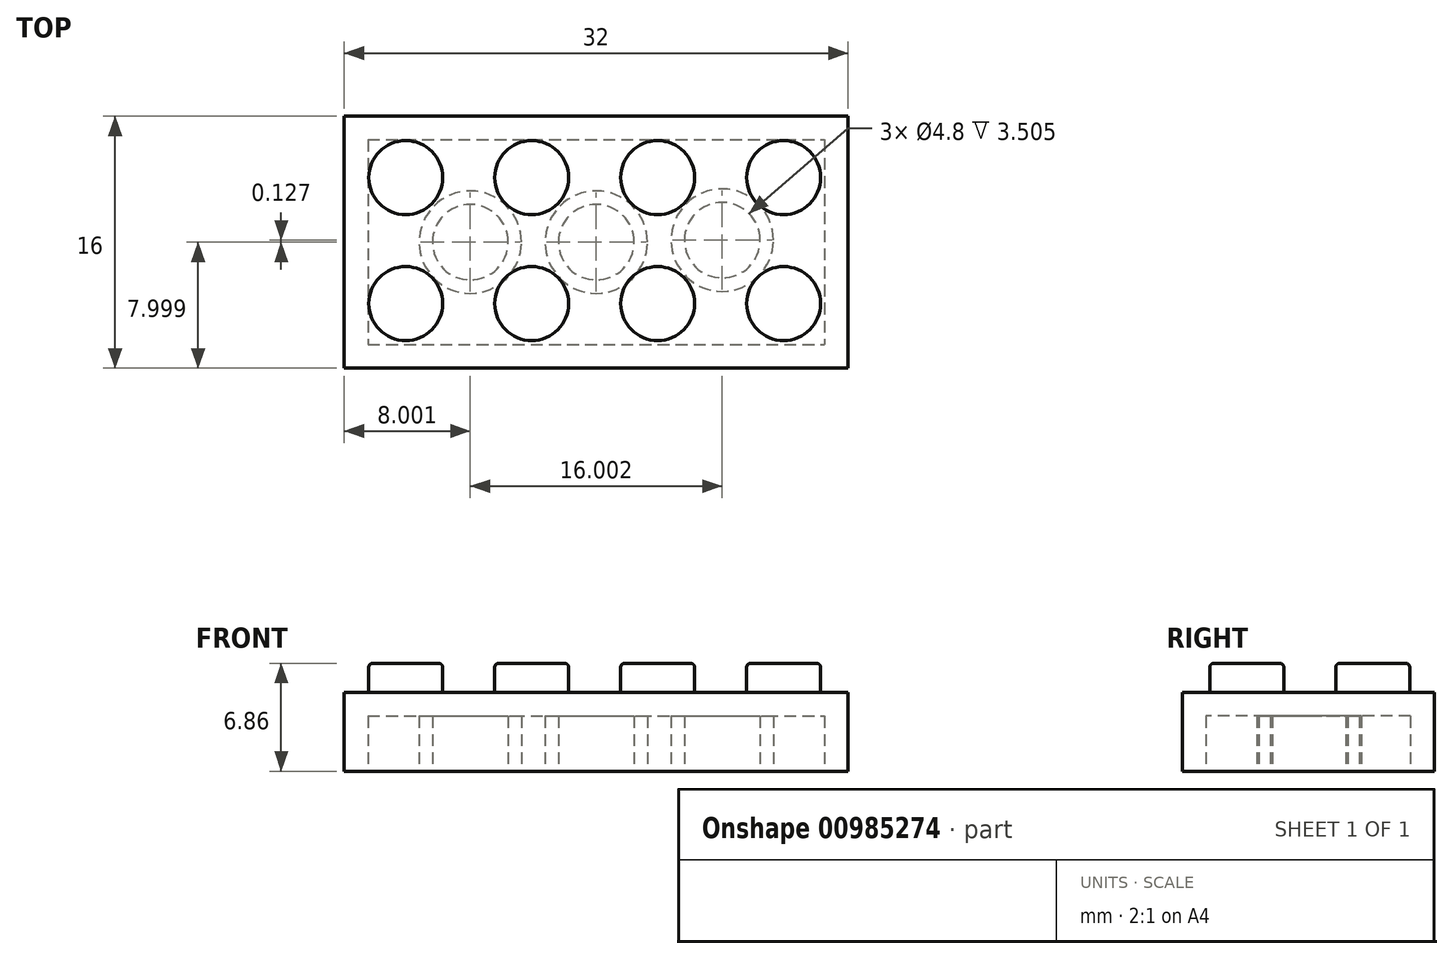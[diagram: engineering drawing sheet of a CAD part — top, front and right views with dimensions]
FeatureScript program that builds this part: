
annotation { "Feature Type Name" : "Feature", "Feature Type Description" : "" }
export const myFeature = defineFeature(function(context is Context, id is Id, definition is map)
    precondition{}
    {
        {
            var Q0;
            Q0=qCreatedBy(makeId("Top.planeOp"),FACE);
            var sketch = newSketch(context, id + "F0", { "sketchPlane" : qUnion([Q0])});
            skLineSegment(sketch, "E0.bottom", {"start": v(0, 0) * mm, "end": v(32, 0) * mm});
            skLineSegment(sketch, "E0.top", {"start": v(0, -16) * mm, "end": v(32, -16) * mm});
            skLineSegment(sketch, "E0.left", {"start": v(0, 0) * mm, "end": v(0, -16) * mm});
            skLineSegment(sketch, "E0.right", {"start": v(32, 0) * mm, "end": v(32, -16) * mm});
            skSolve(sketch);
        }
        {
            var Q0;
            Q0=makeQuery(id+"F0.imprint","IMPRINT",FACE,{"disambiguationData":[TD([[makeQuery(id+"F0.imprint","IMPRINT",EDGE,{"derivedFrom":sQuery(id+"F0.wireOp",EDGE,"E0.bottom")}),-1.0]])]});
            extrude(context, id + "F1", {"entities" : qUnion([Q0]), "depth" : 5 * mm, "offsetDistance" : 25.4 * mm});
        }
        {
            var Q0;
            Q0=makeQuery(id+"F1.opExtrude","CAP_FACE",FACE,{"disambiguationData":[OSD([sQuery(id+"F0.wireOp",EDGE,"E0.bottom"),sQuery(id+"F0.wireOp",EDGE,"E0.top"),sQuery(id+"F0.wireOp",EDGE,"E0.left"),sQuery(id+"F0.wireOp",EDGE,"E0.right")])],"isStart":false});
            var sketch = newSketch(context, id + "F2", { "sketchPlane" : qUnion([Q0])});
            skCircle(sketch, "E1", {"center": v(3.9, -3.9) * mm, "radius": 2.35 * mm});
            skCircle(sketch, "E2.0.1.0", {"center": v(3.9, -11.9) * mm, "radius": 2.35 * mm});
            skCircle(sketch, "E2.1.0.0", {"center": v(11.9, -3.9) * mm, "radius": 2.35 * mm});
            skCircle(sketch, "E2.1.1.0", {"center": v(11.9, -11.9) * mm, "radius": 2.35 * mm});
            skCircle(sketch, "E2.2.0.0", {"center": v(19.9, -3.9) * mm, "radius": 2.35 * mm});
            skCircle(sketch, "E2.2.1.0", {"center": v(19.9, -11.9) * mm, "radius": 2.35 * mm});
            skCircle(sketch, "E2.3.0.0", {"center": v(27.9, -3.9) * mm, "radius": 2.35 * mm});
            skCircle(sketch, "E2.3.1.0", {"center": v(27.9, -11.9) * mm, "radius": 2.35 * mm});
            skLineSegment(sketch, "E2.direction1", {"start": v(3.9, -3.9) * mm, "end": v(11.9, -3.9) * mm, "construction": true});
            skLineSegment(sketch, "E2.direction2", {"start": v(3.9, -3.9) * mm, "end": v(3.9, -11.9) * mm, "construction": true});
            skSolve(sketch);
        }
        {
            var Q0;
            Q0=makeQuery(id+"F2.imprint","IMPRINT",FACE,{"disambiguationData":[TD([[makeQuery(id+"F2.imprint","IMPRINT",EDGE,{"derivedFrom":sQuery(id+"F2.wireOp",EDGE,"E1")}),1.0]])]});
            var Q1;
            Q1=makeQuery(id+"F2.imprint","IMPRINT",FACE,{"disambiguationData":[TD([[makeQuery(id+"F2.imprint","IMPRINT",EDGE,{"derivedFrom":sQuery(id+"F2.wireOp",EDGE,"E2.1.0.0")}),1.0]])]});
            var Q2;
            Q2=makeQuery(id+"F2.imprint","IMPRINT",FACE,{"disambiguationData":[TD([[makeQuery(id+"F2.imprint","IMPRINT",EDGE,{"derivedFrom":sQuery(id+"F2.wireOp",EDGE,"E2.2.0.0")}),1.0]])]});
            var Q3;
            Q3=makeQuery(id+"F2.imprint","IMPRINT",FACE,{"disambiguationData":[TD([[makeQuery(id+"F2.imprint","IMPRINT",EDGE,{"derivedFrom":sQuery(id+"F2.wireOp",EDGE,"E2.3.0.0")}),1.0]])]});
            var Q4;
            Q4=makeQuery(id+"F2.imprint","IMPRINT",FACE,{"disambiguationData":[TD([[makeQuery(id+"F2.imprint","IMPRINT",EDGE,{"derivedFrom":sQuery(id+"F2.wireOp",EDGE,"E2.3.1.0")}),1.0]])]});
            var Q5;
            Q5=makeQuery(id+"F2.imprint","IMPRINT",FACE,{"disambiguationData":[TD([[makeQuery(id+"F2.imprint","IMPRINT",EDGE,{"derivedFrom":sQuery(id+"F2.wireOp",EDGE,"E2.2.1.0")}),1.0]])]});
            var Q6;
            Q6=makeQuery(id+"F2.imprint","IMPRINT",FACE,{"disambiguationData":[TD([[makeQuery(id+"F2.imprint","IMPRINT",EDGE,{"derivedFrom":sQuery(id+"F2.wireOp",EDGE,"E2.1.1.0")}),1.0]])]});
            var Q7;
            Q7=makeQuery(id+"F2.imprint","IMPRINT",FACE,{"disambiguationData":[TD([[makeQuery(id+"F2.imprint","IMPRINT",EDGE,{"derivedFrom":sQuery(id+"F2.wireOp",EDGE,"E2.0.1.0")}),1.0]])]});
            extrude(context, id + "F3", {"entities" : qUnion([Q0, Q1, Q2, Q3, Q4, Q5, Q6, Q7]), "operationType" : NewBodyOperationType.ADD, "depth" : 1.85 * mm, "offsetDistance" : 25.4 * mm});
        }
        {
            var Q0;
            Q0=makeQuery(id+"F3.opExtrude","CAP_EDGE",EDGE,{"disambiguationData":[OSD([sQuery(id+"F2.wireOp",EDGE,"E2.0.1.0")])],"isStart":false});
            var Q1;
            Q1=makeQuery(id+"F3.opExtrude","CAP_EDGE",EDGE,{"disambiguationData":[OSD([sQuery(id+"F2.wireOp",EDGE,"E1")])],"isStart":false});
            var Q2;
            Q2=makeQuery(id+"F3.opExtrude","CAP_EDGE",EDGE,{"disambiguationData":[OSD([sQuery(id+"F2.wireOp",EDGE,"E2.1.0.0")])],"isStart":false});
            var Q3;
            Q3=makeQuery(id+"F3.opExtrude","CAP_EDGE",EDGE,{"disambiguationData":[OSD([sQuery(id+"F2.wireOp",EDGE,"E2.1.1.0")])],"isStart":false});
            var Q4;
            Q4=makeQuery(id+"F3.opExtrude","CAP_EDGE",EDGE,{"disambiguationData":[OSD([sQuery(id+"F2.wireOp",EDGE,"E2.2.1.0")])],"isStart":false});
            var Q5;
            Q5=makeQuery(id+"F3.opExtrude","CAP_EDGE",EDGE,{"disambiguationData":[OSD([sQuery(id+"F2.wireOp",EDGE,"E2.2.0.0")])],"isStart":false});
            var Q6;
            Q6=makeQuery(id+"F3.opExtrude","CAP_EDGE",EDGE,{"disambiguationData":[OSD([sQuery(id+"F2.wireOp",EDGE,"E2.3.0.0")])],"isStart":false});
            var Q7;
            Q7=makeQuery(id+"F3.opExtrude","CAP_EDGE",EDGE,{"disambiguationData":[OSD([sQuery(id+"F2.wireOp",EDGE,"E2.3.1.0")])],"isStart":false});
            fillet(context, id + "F4", {"entities" : qUnion([Q0, Q1, Q2, Q3, Q4, Q5, Q6, Q7]), "radius" : 0.25 * mm, "tangentPropagation" : true, "allowEdgeOverflow" : false});
        }
        {
            var Q0;
            Q0=makeQuery(id+"F1.opExtrude","CAP_FACE",FACE,{"disambiguationData":[OSD([sQuery(id+"F0.wireOp",EDGE,"E0.bottom"),sQuery(id+"F0.wireOp",EDGE,"E0.top"),sQuery(id+"F0.wireOp",EDGE,"E0.left"),sQuery(id+"F0.wireOp",EDGE,"E0.right")])],"isStart":true});
            var sketch = newSketch(context, id + "F5", { "sketchPlane" : qUnion([Q0])});
            skLineSegment(sketch, "E3.0", {"start": v(1.5, 14.5) * mm, "end": v(30.5, 14.5) * mm});
            skLineSegment(sketch, "E3.1", {"start": v(1.5, 1.5) * mm, "end": v(1.5, 14.5) * mm});
            skLineSegment(sketch, "E3.2", {"start": v(1.5, 1.5) * mm, "end": v(30.5, 1.5) * mm});
            skLineSegment(sketch, "E3.3", {"start": v(30.5, 1.5) * mm, "end": v(30.5, 14.5) * mm});
            skLineSegment(sketch, "E4", {"start": v(0, 16) * mm, "end": v(32, 0) * mm, "construction": true});
            skLineSegment(sketch, "E5", {"start": v(0, 0) * mm, "end": v(32, 16) * mm, "construction": true});
            skCircle(sketch, "E6", {"center": v(16, 8) * mm, "radius": 3.25 * mm});
            skCircle(sketch, "E7", {"center": v(16, 8) * mm, "radius": 2.4 * mm});
            skCircle(sketch, "E8", {"center": v(8, 8) * mm, "radius": 3.25 * mm});
            skPoint(sketch, "E8.centerSnap0", {"position": v(1.5, 8) * mm});
            skCircle(sketch, "E9", {"center": v(8, 8) * mm, "radius": 2.4 * mm});
            skCircle(sketch, "E10", {"center": v(24, 7.87) * mm, "radius": 3.25 * mm});
            skCircle(sketch, "E11", {"center": v(24, 7.87) * mm, "radius": 2.4 * mm});
            skSolve(sketch);
        }
        {
            var Q0;
            Q0=makeQuery(id+"F5.imprint","IMPRINT",FACE,{"disambiguationData":[TD([[makeQuery(id+"F5.imprint","IMPRINT",EDGE,{"derivedFrom":sQuery(id+"F5.wireOp",EDGE,"E3.0")}),-1.0]])]});
            var Q1;
            Q1=makeQuery(id+"F5.imprint","IMPRINT",FACE,{"disambiguationData":[TD([[makeQuery(id+"F5.imprint","IMPRINT",EDGE,{"derivedFrom":sQuery(id+"F5.wireOp",EDGE,"E9")}),1.0]])]});
            var Q2;
            Q2=makeQuery(id+"F5.imprint","IMPRINT",FACE,{"disambiguationData":[TD([[makeQuery(id+"F5.imprint","IMPRINT",EDGE,{"derivedFrom":sQuery(id+"F5.wireOp",EDGE,"E7")}),1.0]])]});
            var Q3;
            Q3=makeQuery(id+"F5.imprint","IMPRINT",FACE,{"disambiguationData":[TD([[makeQuery(id+"F5.imprint","IMPRINT",EDGE,{"derivedFrom":sQuery(id+"F5.wireOp",EDGE,"E11")}),1.0]])]});
            extrude(context, id + "F6", {"entities" : qUnion([Q0, Q1, Q2, Q3]), "operationType" : NewBodyOperationType.REMOVE, "oppositeDirection" : true, "depth" : 3.5 * mm, "offsetDistance" : 25.4 * mm});
        }
    });
